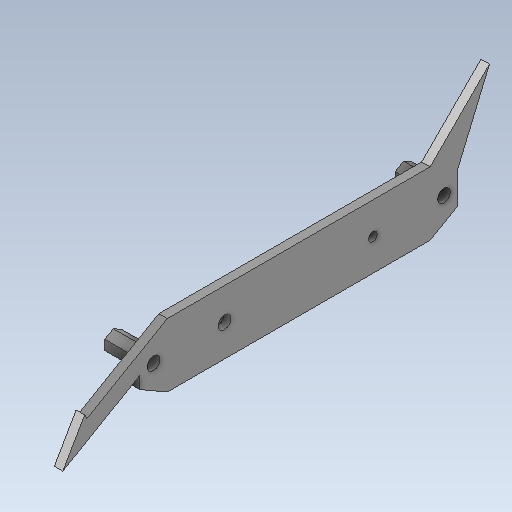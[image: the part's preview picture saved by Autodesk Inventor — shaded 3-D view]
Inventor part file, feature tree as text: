
AUTODESK INVENTOR PART (.ipt)
format: ipt  version: 2020 (Build 240168000, 168)  size: 166,400 bytes
history: native  units: in
note: dims shown in document units (in); Inventor stores cm internally (conversion verified against a paired STEP export)
features: other x3, extrude x2, sketch x2
ambient origin geometry x8: Origin, YZ Plane, XZ Plane, XY Plane, X Axis, Y Axis, Z Axis, Center Point
bodies: Solid1 (feature_tree)
feature tree (7):
  other  "HexWheelGuard.ipt"
  extrude  "Extrusion1"  Depth=0.315in
  extrude  "Extrusion2"  Depth=0.3937in
  other  "Solid1::HexWheelGuard.ipt"
  other  "TaggingFeature2"
  sketch  "Sketch1"  dims[d1=0.3937in d2=0.315in]
  sketch  "Sketch2"  dims[d3=60.0deg d4=1.4843in d5=0.0787in d6=0.3937in d7=0.0in d10=0.5906in d11=1.1024in d12=0.3937in d13=0.0in]
